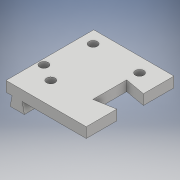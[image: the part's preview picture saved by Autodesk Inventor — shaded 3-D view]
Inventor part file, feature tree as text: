
AUTODESK INVENTOR PART (.ipt)
format: ipt  version: 2017 (Build 210142000, 142)  size: 450,560 bytes
history: native  units: mm
features: extrude x39, sketch x39, shell x1
ambient origin geometry x8: Origin, YZ Plane, XZ Plane, XY Plane, X Axis, Y Axis, Z Axis, Center Point
bodies: Solid1 (feature_tree)
feature tree (79):
  extrude  "Extrusion1"  Depth=35.0mm
  shell  "Shell1"  Thickness=20.0mm
  extrude  "Extrusion2"  Depth=55.0mm
  extrude  "Extrusion3"  TaperAngle=0.0deg  [1 undecoded]
  extrude  "Extrusion4"  Depth=5.0mm
  extrude  "Extrusion5"  TaperAngle=0.0deg  [1 undecoded]
  extrude  "Extrusion6"  Depth=10.0mm TaperAngle=0.0deg
  extrude  "Extrusion7"  Depth=15.0mm TaperAngle=0.0deg
  extrude  "Extrusion9"  Depth=8.5mm
  extrude  "Extrusion10"  Depth=15.0mm TaperAngle=0.0deg
  extrude  "Extrusion11"  Depth=35.46mm
  extrude  "Extrusion12"  Depth=15.0mm TaperAngle=0.0deg
  extrude  "Extrusion13"  Depth=4.5mm
  extrude  "Extrusion14"  Depth=15.0mm TaperAngle=0.0deg
  extrude  "Extrusion15"  Depth=8.5mm
  extrude  "Extrusion16"  Depth=15.0mm TaperAngle=0.0deg
  extrude  "Extrusion17"  Depth=28.505mm
  extrude  "Extrusion18"  Depth=15.0mm TaperAngle=0.0deg
  extrude  "Extrusion19"  Depth=36.0mm
  extrude  "Extrusion20"  Depth=15.0mm TaperAngle=0.0deg
  extrude  "Extrusion23"  Depth=5.0mm
  extrude  "Extrusion21"  Depth=4.1656mm
  extrude  "Extrusion22"  Depth=35.46mm
  extrude  "Extrusion24"  Depth=10.0mm
  extrude  "Extrusion25"  Depth=10.0mm TaperAngle=0.0deg
  extrude  "Extrusion26"  Depth=2.583mm TaperAngle=0.0deg
  extrude  "Extrusion27"  Depth=2.583mm TaperAngle=0.0deg
  extrude  "Extrusion28"  Depth=100.0mm TaperAngle=0.0deg
  extrude  "Extrusion29"  Depth=5.0mm
  extrude  "Extrusion30"  Depth=1.0mm
  extrude  "Extrusion31"  Depth=5.0mm
  extrude  "Extrusion32"  Depth=4.1656mm
  extrude  "Extrusion33"  Depth=6.161mm
  extrude  "Extrusion34"  Depth=4.1656mm
  extrude  "Extrusion35"  Depth=15.906mm
  extrude  "Extrusion36"  Depth=22.5mm TaperAngle=0.0deg
  extrude  "Extrusion37"  Depth=22.5mm TaperAngle=0.0deg
  extrude  "Extrusion38"  Depth=4.0mm
  extrude  "Extrusion39"  TaperAngle=0.0deg  [1 undecoded]
  extrude  "Extrusion40"  Depth=5.0mm
  sketch  "Sketch1"  dims[d0=35.0mm d1=37.0mm d2=20.0mm]
  sketch  "Sketch2"  dims[d3=11.0mm d4=55.0mm]
  sketch  "Sketch3"  dims[d5=26.0mm d6=0.0mm]
  sketch  "Sketch4"  dims[d7=50.0mm d8=0.0mm d9=5.0mm]
  sketch  "Sketch5"  dims[d10=17.0mm d11=0.0mm]
  sketch  "Sketch6"  dims[d12=11.0mm d13=10.0mm d14=0.0mm]
  sketch  "Sketch7"  dims[d15=15.0mm d16=0.0mm d17=15.0mm d18=0.0mm]
  sketch  "Sketch13"  dims[d19=4.1656mm d20=8.5mm]
  sketch  "Sketch14"  dims[d21=11.5mm d22=15.0mm d23=0.0mm]
  sketch  "Sketch15"  dims[d24=4.1656mm d25=35.46mm]
  sketch  "Sketch16"  dims[d26=23.505mm d27=15.0mm d28=0.0mm]
  sketch  "Sketch17"  dims[d29=4.1656mm d30=4.5mm]
  sketch  "Sketch18"  dims[d31=14.0mm d32=15.0mm d33=0.0mm]
  sketch  "Sketch20"  dims[d41=4.1656mm d42=8.5mm]
  sketch  "Sketch21"  dims[d43=11.5mm d44=15.0mm d45=0.0mm]
  sketch  "Sketch22"  dims[d46=4.1656mm d47=28.505mm]
  sketch  "Sketch23"  dims[d48=35.46mm d49=15.0mm d50=0.0mm]
  sketch  "Sketch24"  dims[d51=4.1656mm d52=36.0mm]
  sketch  "Sketch25"  dims[d53=4.5mm d54=15.0mm d55=0.0mm]
  sketch  "Sketch26"  dims[d56=5.0mm d57=50.0mm]
  sketch  "Sketch27"  dims[d58=21.0mm d59=0.0mm d60=4.1656mm]
  sketch  "Sketch28"  dims[d61=23.505mm d62=35.46mm]
  sketch  "Sketch29"  dims[d63=10.0mm d64=0.0mm d65=4.1656mm]
  sketch  "Sketch30"  dims[d67=36.0mm d68=10.0mm d69=0.0mm]
  sketch  "Sketch31"  dims[d70=4.5mm d71=2.583mm d72=0.0mm]
  sketch  "Sketch33"  dims[d73=2.583mm d74=0.0mm d75=2.583mm d76=0.0mm]
  sketch  "Sketch34"  dims[d77=6.917mm d78=100.0mm d79=0.0mm]
  sketch  "Sketch35"  dims[d80=5.0mm d81=5.0mm]
  sketch  "Sketch36"  dims[d83=1.0mm d84=1.0mm]
  sketch  "Sketch38"  dims[d88=22.5mm d89=0.0mm d90=4.1656mm]
  sketch  "Sketch40"  dims[d93=25.0mm d94=0.0mm d95=4.1656mm]
  sketch  "Sketch41"  dims[d96=2.702mm d97=15.906mm]
  sketch  "Sketch44"  dims[d102=2.5mm d103=22.5mm d104=0.0mm]
  sketch  "Sketch45"  dims[d105=9.0mm d106=4.0mm]
  sketch  "Sketch46"  dims[d107=5.0mm d108=0.0mm]
  sketch  "Sketch47"  dims[d109=30.0mm d110=0.0mm d111=4.1656mm d112=6.083mm d113=4.0mm d114=30.0mm d115=0.0mm d116=30.0mm d117=0.0mm d118=30.0mm d119=0.0mm d120=30.0mm d121=0.0mm d122=10.0mm d123=0.0mm d124=8.6943mm d125=13.962634mm d126=29.670597mm d127=5.0mm d130=5.0mm d131=34.389mm d132=10.0mm d133=0.0mm d134=10.0mm d135=0.0mm d136=8.6943mm d137=13.962634mm d138=29.670597mm d139=5.0mm d140=0.0mm d141=8.694mm d142=37.0mm d143=0.0mm d144=32.0mm d145=0.0mm d146=5.0mm d147=27.0mm d148=0.0mm d149=8.6943mm d150=13.962634mm d151=29.670597mm d152=5.0mm d153=0.0mm d154=9.187mm d155=5.0mm d156=0.0mm d157=15.0mm d158=15.0mm d159=13.083mm d160=13.962634mm d161=13.962634mm d162=10.0mm d163=10.0mm d164=0.0mm d165=10.0mm d166=0.0mm d167=4.1656mm d168=11.0mm d169=11.0mm d170=10.0mm d171=0.0mm d172=3.0mm d173=1.0mm d174=7.0mm d175=5.0mm d176=5.0mm d177=0.0mm]
  sketch  "Sketch37"  dims[d85=100.0mm d86=0.0mm d87=5.0mm]
  sketch  "Sketch39"  dims[d91=5.851mm d92=6.161mm]
  sketch  "Sketch43"  dims[d98=25.0mm d99=0.0mm d100=22.5mm d101=0.0mm]
note: 3 required parameter values undecoded (feature->parameter linkage not recoverable at this tier; creation-order binding heuristic only, values carry confidence <= 0.55)
